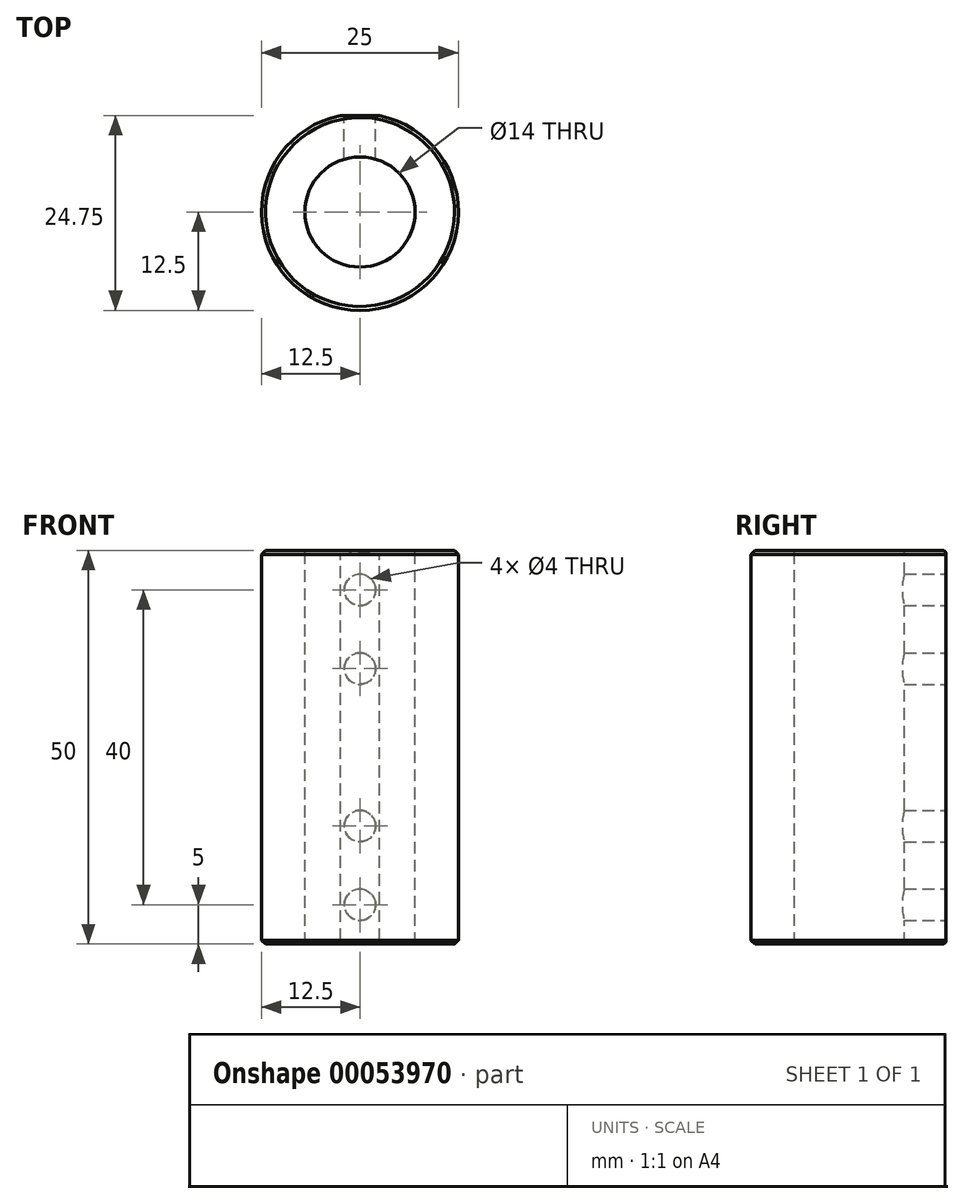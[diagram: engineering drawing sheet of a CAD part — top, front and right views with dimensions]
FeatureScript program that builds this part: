
annotation { "Feature Type Name" : "Feature", "Feature Type Description" : "" }
export const myFeature = defineFeature(function(context is Context, id is Id, definition is map)
    precondition{}
    {
        {
            var Q0;
            Q0=qCreatedBy(makeId("Top.planeOp"),FACE);
            var sketch = newSketch(context, id + "F0", { "sketchPlane" : qUnion([Q0])});
            skCircle(sketch, "E0", {"center": v(0, 0) * mm, "radius": 12.5 * mm});
            skSolve(sketch);
        }
        {
            var Q0;
            Q0 = qSketchRegion(id + "F0", true);
            extrude(context, id + "F1", {"entities" : qUnion([Q0]), "depth" : 50 * mm});
        }
        {
            var Q0;
            Q0=makeQuery(id+"F1.opExtrude","CAP_FACE",FACE,{"disambiguationData":[OSD([sQuery(id+"F0.wireOp",EDGE,"E0")])],"isStart":false});
            var sketch = newSketch(context, id + "F2", { "sketchPlane" : qUnion([Q0])});
            skCircle(sketch, "E1", {"center": v(0, 0) * mm, "radius": 7 * mm});
            skSolve(sketch);
        }
        {
            var Q0;
            Q0 = qSketchRegion(id + "F2", true);
            extrude(context, id + "F3", {"entities" : qUnion([Q0]), "operationType" : NewBodyOperationType.REMOVE, "oppositeDirection" : true, "depth" : 50 * mm});
        }
        {
            var Q0;
            Q0=makeQuery(id+"F1.opExtrude","CAP_FACE",FACE,{"disambiguationData":[OSD([sQuery(id+"F0.wireOp",EDGE,"E0")])],"isStart":false});
            var sketch = newSketch(context, id + "F4", { "sketchPlane" : qUnion([Q0])});
            skLineSegment(sketch, "E2", {"start": v(-2.5, 12.25) * mm, "end": v(2.5, 12.25) * mm});
            skLineSegment(sketch, "E3", {"start": v(-2.5, 12.25) * mm, "end": v(0, 12.76) * mm});
            skLineSegment(sketch, "E4", {"start": v(0, 12.76) * mm, "end": v(2.5, 12.25) * mm});
            skSolve(sketch);
        }
        {
            var Q0;
            Q0 = qSketchRegion(id + "F4", true);
            extrude(context, id + "F5", {"entities" : qUnion([Q0]), "operationType" : NewBodyOperationType.REMOVE, "oppositeDirection" : true, "depth" : 50 * mm});
        }
        {
            var Q0;
            Q0=makeQuery(id+"F5.boolean.opBoolean","COPY",FACE,{"derivedFrom":makeQuery(id+"F5.opExtrude","SWEPT_FACE",FACE,{"disambiguationData":[OSD([sQuery(id+"F4.wireOp",EDGE,"E2")])]})});
            var sketch = newSketch(context, id + "F6", { "sketchPlane" : qUnion([Q0])});
            skCircle(sketch, "E5", {"center": v(0, 5) * mm, "radius": 2 * mm});
            skCircle(sketch, "E6", {"center": v(0, 15) * mm, "radius": 2 * mm});
            skCircle(sketch, "E7", {"center": v(0, 45) * mm, "radius": 2 * mm});
            skCircle(sketch, "E8", {"center": v(0, 35) * mm, "radius": 2 * mm});
            skSolve(sketch);
        }
        {
            var Q0;
            Q0 = qSketchRegion(id + "F6", true);
            extrude(context, id + "F7", {"entities" : qUnion([Q0]), "operationType" : NewBodyOperationType.REMOVE, "oppositeDirection" : true, "depth" : 10 * mm});
        }
        {
            var Q0;
            Q0=makeQuery(id+"F1.opExtrude","CAP_EDGE",EDGE,{"disambiguationData":[OSD([sQuery(id+"F0.wireOp",EDGE,"E0")])],"isStart":false});
            var Q1;
            Q1=makeQuery(id+"F3.boolean.opBoolean","COPY",EDGE,{"derivedFrom":makeQuery(id+"F3.opExtrude","CAP_EDGE",EDGE,{"disambiguationData":[OSD([sQuery(id+"F2.wireOp",EDGE,"E1")])],"isStart":true})});
            var Q2;
            Q2=makeQuery(id+"F3.boolean.opBoolean","COPY",EDGE,{"derivedFrom":makeQuery(id+"F3.opExtrude","CAP_EDGE",EDGE,{"disambiguationData":[OSD([sQuery(id+"F2.wireOp",EDGE,"E1")])],"isStart":false})});
            var Q3;
            Q3=makeQuery(id+"F1.opExtrude","CAP_EDGE",EDGE,{"disambiguationData":[OSD([sQuery(id+"F0.wireOp",EDGE,"E0")])],"isStart":true});
            chamfer(context, id + "F8", {"entities" : qUnion([Q0, Q1, Q2, Q3]), "width" : 0.5 * mm, "tangentPropagation" : true});
        }
    });
